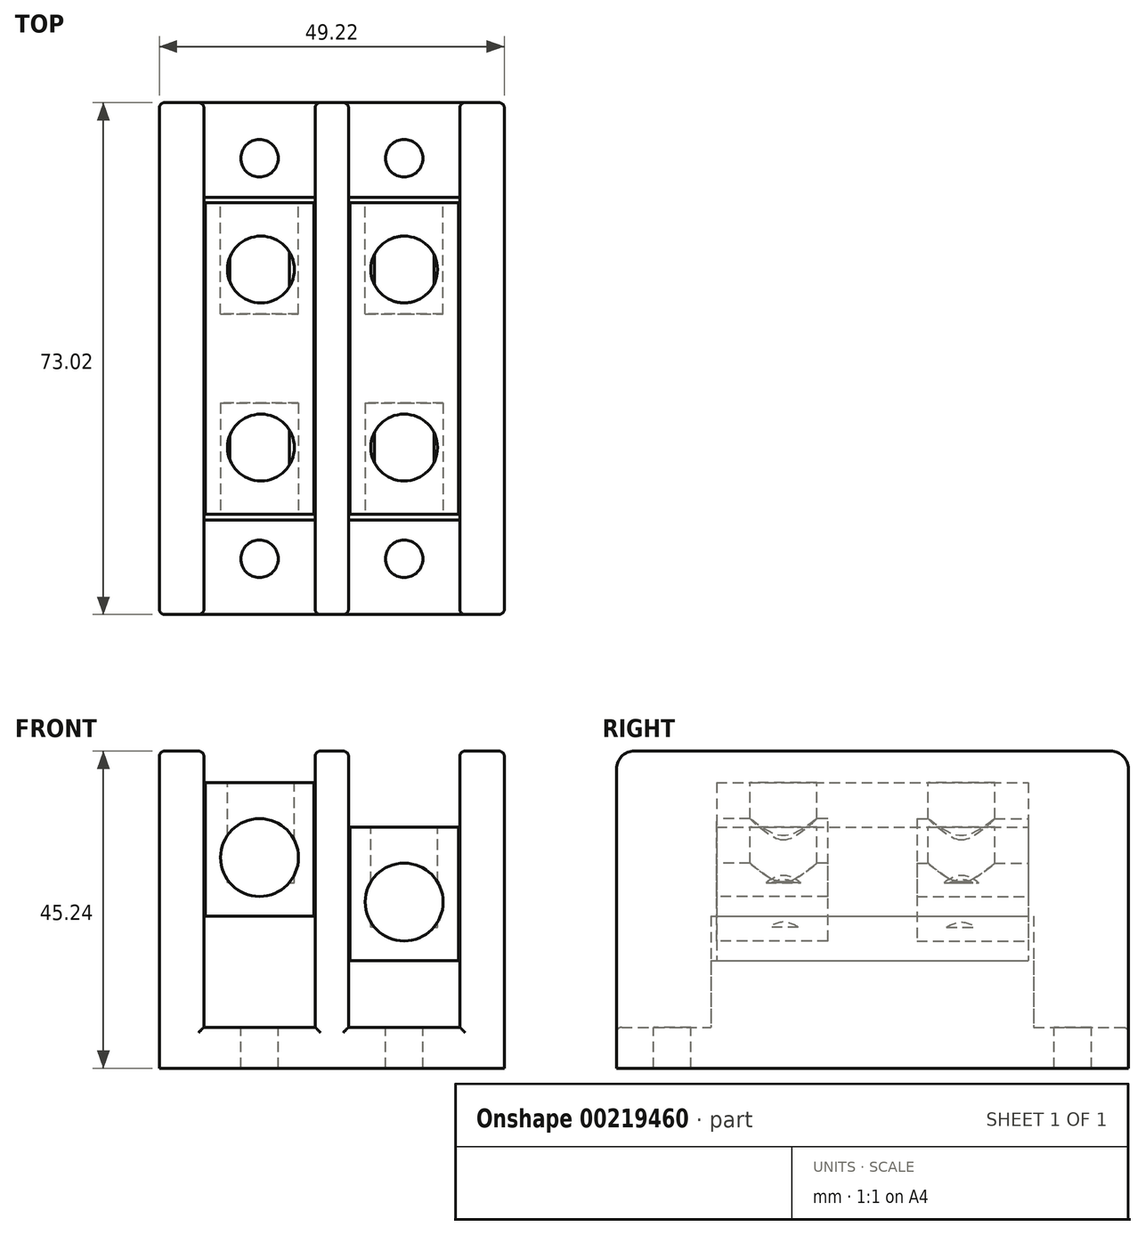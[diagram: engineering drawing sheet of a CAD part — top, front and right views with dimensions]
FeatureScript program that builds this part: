
annotation { "Feature Type Name" : "Feature", "Feature Type Description" : "" }
export const myFeature = defineFeature(function(context is Context, id is Id, definition is map)
    precondition{}
    {
        {
            var Q0;
            Q0=qCreatedBy(makeId("Top.planeOp"),FACE);
            var sketch = newSketch(context, id + "F0", { "sketchPlane" : qUnion([Q0])});
            skLineSegment(sketch, "E0.bottom", {"start": v(-24.6, -36.51) * mm, "end": v(24.6, -36.51) * mm});
            skLineSegment(sketch, "E0.top", {"start": v(-24.6, 36.51) * mm, "end": v(24.6, 36.51) * mm});
            skLineSegment(sketch, "E0.left", {"start": v(-24.6, -36.51) * mm, "end": v(-24.6, 36.51) * mm});
            skLineSegment(sketch, "E0.right", {"start": v(24.6, -36.51) * mm, "end": v(24.6, 36.51) * mm});
            skPoint(sketch, "E0.middle", {"position": v(0, 0) * mm});
            skSolve(sketch);
        }
        {
            var Q0;
            Q0=qSketchRegion(id+"F0",true);
            extrude(context, id + "F1", {"entities" : qUnion([Q0]), "depth" : 45.24 * mm});
        }
        {
            var Q0;
            Q0=makeQuery(id+"F1.opExtrude","CAP_FACE",FACE,{"disambiguationData":[OSD([sQuery(id+"F0.wireOp",EDGE,"E0.bottom"),sQuery(id+"F0.wireOp",EDGE,"E0.top"),sQuery(id+"F0.wireOp",EDGE,"E0.left"),sQuery(id+"F0.wireOp",EDGE,"E0.right")])],"isStart":false});
            var sketch = newSketch(context, id + "F2", { "sketchPlane" : qUnion([Q0])});
            skLineSegment(sketch, "E1.bottom", {"start": v(-2.38, -36.51) * mm, "end": v(-18.26, -36.51) * mm});
            skLineSegment(sketch, "E1.top", {"start": v(-2.38, 36.51) * mm, "end": v(-18.26, 36.51) * mm});
            skLineSegment(sketch, "E1.left", {"start": v(-2.38, -36.51) * mm, "end": v(-2.38, 36.51) * mm});
            skLineSegment(sketch, "E1.right", {"start": v(-18.26, -36.51) * mm, "end": v(-18.26, 36.51) * mm});
            skPoint(sketch, "E1.middle", {"position": v(-10.32, 0) * mm});
            skPoint(sketch, "E2.middle", {"position": v(0, 0) * mm});
            skLineSegment(sketch, "E3.bottom", {"start": v(18.26, -36.51) * mm, "end": v(2.38, -36.51) * mm});
            skLineSegment(sketch, "E3.top", {"start": v(18.26, 36.51) * mm, "end": v(2.38, 36.51) * mm});
            skLineSegment(sketch, "E3.left", {"start": v(18.26, -36.51) * mm, "end": v(18.26, 36.51) * mm});
            skLineSegment(sketch, "E3.right", {"start": v(2.38, -36.51) * mm, "end": v(2.38, 36.51) * mm});
            skPoint(sketch, "E3.middle", {"position": v(10.32, 0) * mm});
            skSolve(sketch);
        }
        {
            var Q0;
            Q0=qSketchRegion(id+"F2",true);
            extrude(context, id + "F3", {"entities" : qUnion([Q0]), "operationType" : NewBodyOperationType.REMOVE, "oppositeDirection" : true, "depth" : 39.4 * mm});
        }
        {
            var Q0;
            Q0=makeQuery(id+"F3.boolean.opBoolean","COPY",FACE,{"derivedFrom":makeQuery(id+"F3.opExtrude","CAP_FACE",FACE,{"disambiguationData":[OSD([sQuery(id+"F2.wireOp",EDGE,"E1.bottom"),sQuery(id+"F2.wireOp",EDGE,"E1.top"),sQuery(id+"F2.wireOp",EDGE,"E1.left"),sQuery(id+"F2.wireOp",EDGE,"E1.right")])],"isStart":false})});
            var sketch = newSketch(context, id + "F4", { "sketchPlane" : qUnion([Q0])});
            skCircle(sketch, "E4", {"center": v(-10.32, 28.58) * mm, "radius": 2.67 * mm});
            skCircle(sketch, "E5", {"center": v(-10.32, -28.58) * mm, "radius": 2.67 * mm});
            skCircle(sketch, "E6", {"center": v(10.32, 28.58) * mm, "radius": 2.67 * mm});
            skCircle(sketch, "E7", {"center": v(10.32, -28.58) * mm, "radius": 2.67 * mm});
            skSolve(sketch);
        }
        {
            var Q0;
            Q0=qSketchRegion(id+"F4",true);
            extrude(context, id + "F5", {"entities" : qUnion([Q0]), "operationType" : NewBodyOperationType.REMOVE, "oppositeDirection" : true, "depth" : 5.84 * mm});
        }
        {
            var Q0;
            {var subQ0=sQuery(id+"F0.wireOp",EDGE,"E0.left");var subQ1=sQuery(id+"F0.wireOp",EDGE,"E0.top");Q0=makeQuery(id+"F3.boolean.opBoolean","SPLIT",EDGE,{"disambiguationData":[TD([makeQuery(id+"F1.opExtrude","SWEPT_FACE",FACE,{"disambiguationData":[OSD([subQ0])]})])],"derivedFrom":makeQuery(id+"F1.opExtrude","CAP_EDGE",EDGE,{"disambiguationData":[OSD([subQ1])],"isStart":false})});}
            var Q1;
            {var subQ0=sQuery(id+"F0.wireOp",EDGE,"E0.top");Q1=makeQuery(id+"F3.boolean.opBoolean","SPLIT",EDGE,{"disambiguationData":[TD([makeQuery(id+"F3.opExtrude","SWEPT_FACE",FACE,{"disambiguationData":[OSD([sQuery(id+"F2.wireOp",EDGE,"E1.left")])]})])],"derivedFrom":makeQuery(id+"F1.opExtrude","CAP_EDGE",EDGE,{"disambiguationData":[OSD([subQ0])],"isStart":false})});}
            var Q2;
            {var subQ0=sQuery(id+"F0.wireOp",EDGE,"E0.right");var subQ1=sQuery(id+"F0.wireOp",EDGE,"E0.top");Q2=makeQuery(id+"F3.boolean.opBoolean","SPLIT",EDGE,{"disambiguationData":[TD([makeQuery(id+"F1.opExtrude","SWEPT_FACE",FACE,{"disambiguationData":[OSD([subQ0])]})])],"derivedFrom":makeQuery(id+"F1.opExtrude","CAP_EDGE",EDGE,{"disambiguationData":[OSD([subQ1])],"isStart":false})});}
            var Q3;
            {var subQ0=sQuery(id+"F0.wireOp",EDGE,"E0.bottom");var subQ1=sQuery(id+"F0.wireOp",EDGE,"E0.left");Q3=makeQuery(id+"F3.boolean.opBoolean","SPLIT",EDGE,{"disambiguationData":[TD([makeQuery(id+"F1.opExtrude","SWEPT_FACE",FACE,{"disambiguationData":[OSD([subQ1])]})])],"derivedFrom":makeQuery(id+"F1.opExtrude","CAP_EDGE",EDGE,{"disambiguationData":[OSD([subQ0])],"isStart":false})});}
            var Q4;
            {var subQ0=sQuery(id+"F0.wireOp",EDGE,"E0.bottom");Q4=makeQuery(id+"F3.boolean.opBoolean","SPLIT",EDGE,{"disambiguationData":[TD([makeQuery(id+"F3.opExtrude","SWEPT_FACE",FACE,{"disambiguationData":[OSD([sQuery(id+"F2.wireOp",EDGE,"E1.left")])]})])],"derivedFrom":makeQuery(id+"F1.opExtrude","CAP_EDGE",EDGE,{"disambiguationData":[OSD([subQ0])],"isStart":false})});}
            var Q5;
            {var subQ0=sQuery(id+"F0.wireOp",EDGE,"E0.bottom");var subQ1=sQuery(id+"F0.wireOp",EDGE,"E0.right");Q5=makeQuery(id+"F3.boolean.opBoolean","SPLIT",EDGE,{"disambiguationData":[TD([makeQuery(id+"F1.opExtrude","SWEPT_FACE",FACE,{"disambiguationData":[OSD([subQ1])]})])],"derivedFrom":makeQuery(id+"F1.opExtrude","CAP_EDGE",EDGE,{"disambiguationData":[OSD([subQ0])],"isStart":false})});}
            fillet(context, id + "F6", {"entities" : qUnion([Q0, Q1, Q2, Q3, Q4, Q5]), "radius" : 2.54 * mm, "tangentPropagation" : true});
        }
        {
            var Q0;
            Q0=makeQuery(id+"F3.boolean.opBoolean","COPY",EDGE,{"derivedFrom":makeQuery(id+"F3.opExtrude","CAP_EDGE",EDGE,{"disambiguationData":[OSD([sQuery(id+"F2.wireOp",EDGE,"E1.top")])],"isStart":false})});
            var Q1;
            Q1=makeQuery(id+"F3.boolean.opBoolean","COPY",EDGE,{"derivedFrom":makeQuery(id+"F3.opExtrude","CAP_EDGE",EDGE,{"disambiguationData":[OSD([sQuery(id+"F2.wireOp",EDGE,"E3.top")])],"isStart":false})});
            var Q2;
            Q2=makeQuery(id+"F3.boolean.opBoolean","COPY",EDGE,{"derivedFrom":makeQuery(id+"F3.opExtrude","CAP_EDGE",EDGE,{"disambiguationData":[OSD([sQuery(id+"F2.wireOp",EDGE,"E1.bottom")])],"isStart":false})});
            var Q3;
            Q3=makeQuery(id+"F3.boolean.opBoolean","COPY",EDGE,{"derivedFrom":makeQuery(id+"F3.opExtrude","CAP_EDGE",EDGE,{"disambiguationData":[OSD([sQuery(id+"F2.wireOp",EDGE,"E3.bottom")])],"isStart":false})});
            var Q4;
            Q4=makeQuery(id+"F1.opExtrude","SWEPT_EDGE",EDGE,{"disambiguationData":[OSD([sQuery(id+"F0.wireOp",EDGE,"E0.bottom"),sQuery(id+"F0.wireOp",EDGE,"E0.left")])]});
            var Q5;
            Q5=makeQuery(id+"F3.boolean.opBoolean","COPY",EDGE,{"derivedFrom":makeQuery(id+"F3.opExtrude","SWEPT_EDGE",EDGE,{"disambiguationData":[OSD([sQuery(id+"F0.wireOp",EDGE,"E0.bottom"),sQuery(id+"F2.wireOp",EDGE,"E1.bottom"),sQuery(id+"F2.wireOp",EDGE,"E1.right")])]})});
            var Q6;
            Q6=makeQuery(id+"F3.boolean.opBoolean","COPY",EDGE,{"derivedFrom":makeQuery(id+"F3.opExtrude","SWEPT_EDGE",EDGE,{"disambiguationData":[OSD([sQuery(id+"F0.wireOp",EDGE,"E0.bottom"),sQuery(id+"F2.wireOp",EDGE,"E3.bottom"),sQuery(id+"F2.wireOp",EDGE,"E3.right")])]})});
            var Q7;
            Q7=makeQuery(id+"F1.opExtrude","SWEPT_EDGE",EDGE,{"disambiguationData":[OSD([sQuery(id+"F0.wireOp",EDGE,"E0.bottom"),sQuery(id+"F0.wireOp",EDGE,"E0.right")])]});
            var Q8;
            Q8=makeQuery(id+"F3.boolean.opBoolean","COPY",EDGE,{"derivedFrom":makeQuery(id+"F3.opExtrude","SWEPT_EDGE",EDGE,{"disambiguationData":[OSD([sQuery(id+"F0.wireOp",EDGE,"E0.bottom"),sQuery(id+"F2.wireOp",EDGE,"E3.bottom"),sQuery(id+"F2.wireOp",EDGE,"E3.left")])]})});
            var Q9;
            Q9=makeQuery(id+"F3.boolean.opBoolean","COPY",EDGE,{"derivedFrom":makeQuery(id+"F3.opExtrude","SWEPT_EDGE",EDGE,{"disambiguationData":[OSD([sQuery(id+"F0.wireOp",EDGE,"E0.bottom"),sQuery(id+"F2.wireOp",EDGE,"E1.bottom"),sQuery(id+"F2.wireOp",EDGE,"E1.left")])]})});
            fillet(context, id + "F7", {"entities" : qUnion([Q0, Q1, Q2, Q3, Q4, Q5, Q6, Q7, Q8, Q9]), "radius" : 0.76 * mm, "tangentPropagation" : true});
        }
        {
            var Q0;
            Q0=makeQuery(id+"F3.boolean.opBoolean","COPY",FACE,{"derivedFrom":makeQuery(id+"F3.opExtrude","CAP_FACE",FACE,{"disambiguationData":[OSD([sQuery(id+"F2.wireOp",EDGE,"E1.bottom"),sQuery(id+"F2.wireOp",EDGE,"E1.top"),sQuery(id+"F2.wireOp",EDGE,"E1.left"),sQuery(id+"F2.wireOp",EDGE,"E1.right")])],"isStart":false})});
            var sketch = newSketch(context, id + "F8", { "sketchPlane" : qUnion([Q0])});
            skLineSegment(sketch, "E8.bottom", {"start": v(-18.26, 23.02) * mm, "end": v(-2.38, 23.02) * mm});
            skLineSegment(sketch, "E8.top", {"start": v(-18.26, -23.02) * mm, "end": v(-2.38, -23.02) * mm});
            skLineSegment(sketch, "E8.left", {"start": v(-18.26, 23.02) * mm, "end": v(-18.26, -23.02) * mm});
            skLineSegment(sketch, "E8.right", {"start": v(-2.38, 23.02) * mm, "end": v(-2.38, -23.02) * mm});
            skSolve(sketch);
        }
        {
            var Q0;
            Q0=qSketchRegion(id+"F8",true);
            extrude(context, id + "F9", {"entities" : qUnion([Q0]), "operationType" : NewBodyOperationType.ADD, "depth" : 15.88 * mm});
        }
        {
            var Q0;
            Q0=makeQuery(id+"F3.boolean.opBoolean","COPY",FACE,{"derivedFrom":makeQuery(id+"F3.opExtrude","CAP_FACE",FACE,{"disambiguationData":[OSD([sQuery(id+"F2.wireOp",EDGE,"E3.bottom"),sQuery(id+"F2.wireOp",EDGE,"E3.top"),sQuery(id+"F2.wireOp",EDGE,"E3.left"),sQuery(id+"F2.wireOp",EDGE,"E3.right")])],"isStart":false})});
            var sketch = newSketch(context, id + "F10", { "sketchPlane" : qUnion([Q0])});
            skLineSegment(sketch, "E9.bottom", {"start": v(2.38, 23.02) * mm, "end": v(18.26, 23.02) * mm});
            skLineSegment(sketch, "E9.top", {"start": v(2.38, -23.02) * mm, "end": v(18.26, -23.02) * mm});
            skLineSegment(sketch, "E9.left", {"start": v(2.38, 23.02) * mm, "end": v(2.38, -23.02) * mm});
            skLineSegment(sketch, "E9.right", {"start": v(18.26, 23.02) * mm, "end": v(18.26, -23.02) * mm});
            skSolve(sketch);
        }
        {
            var Q0;
            Q0=qSketchRegion(id+"F10",true);
            extrude(context, id + "F11", {"entities" : qUnion([Q0]), "operationType" : NewBodyOperationType.ADD, "depth" : 9.52 * mm});
        }
        {
            var Q0;
            Q0=makeQuery(id+"F9.opExtrude","CAP_FACE",FACE,{"disambiguationData":[OSD([sQuery(id+"F8.wireOp",EDGE,"E8.bottom"),sQuery(id+"F8.wireOp",EDGE,"E8.top"),sQuery(id+"F8.wireOp",EDGE,"E8.left"),sQuery(id+"F8.wireOp",EDGE,"E8.right")])],"isStart":false});
            var sketch = newSketch(context, id + "F12", { "sketchPlane" : qUnion([Q0])});
            skLineSegment(sketch, "E10.bottom", {"start": v(-18.06, -22.23) * mm, "end": v(-2.58, -22.23) * mm});
            skLineSegment(sketch, "E10.top", {"start": v(-18.06, 22.23) * mm, "end": v(-2.58, 22.23) * mm});
            skLineSegment(sketch, "E10.left", {"start": v(-18.06, -22.23) * mm, "end": v(-18.06, 22.23) * mm});
            skLineSegment(sketch, "E10.right", {"start": v(-2.58, -22.23) * mm, "end": v(-2.58, 22.23) * mm});
            skPoint(sketch, "E10.middle", {"position": v(-10.32, 0) * mm});
            skSolve(sketch);
        }
        {
            var Q0;
            Q0=makeQuery(id+"F12.imprint","IMPRINT",FACE,{"disambiguationData":[TD([[makeQuery(id+"F12.imprint","IMPRINT",EDGE,{"derivedFrom":sQuery(id+"F12.wireOp",EDGE,"E10.bottom")}),1.0]])]});
            extrude(context, id + "F13", {"entities" : qUnion([Q0]), "depth" : 19.05 * mm});
        }
        {
            var Q0;
            Q0=makeQuery(id+"F11.opExtrude","CAP_FACE",FACE,{"disambiguationData":[OSD([sQuery(id+"F10.wireOp",EDGE,"E9.bottom"),sQuery(id+"F10.wireOp",EDGE,"E9.top"),sQuery(id+"F10.wireOp",EDGE,"E9.left"),sQuery(id+"F10.wireOp",EDGE,"E9.right")])],"isStart":false});
            var sketch = newSketch(context, id + "F14", { "sketchPlane" : qUnion([Q0])});
            skLineSegment(sketch, "E11.bottom", {"start": v(2.58, -22.22) * mm, "end": v(18.06, -22.22) * mm});
            skLineSegment(sketch, "E11.top", {"start": v(2.58, 22.23) * mm, "end": v(18.06, 22.23) * mm});
            skLineSegment(sketch, "E11.left", {"start": v(2.58, -22.23) * mm, "end": v(2.58, 22.23) * mm});
            skLineSegment(sketch, "E11.right", {"start": v(18.06, -22.23) * mm, "end": v(18.06, 22.23) * mm});
            skPoint(sketch, "E11.middle", {"position": v(10.32, 0) * mm});
            skSolve(sketch);
        }
        {
            var Q0;
            Q0=qSketchRegion(id+"F14",true);
            extrude(context, id + "F15", {"entities" : qUnion([Q0]), "depth" : 19.05 * mm});
        }
        {
            var Q0;
            Q0=makeQuery(id+"F13.opExtrude","CAP_FACE",FACE,{"disambiguationData":[OSD([sQuery(id+"F12.wireOp",EDGE,"E10.bottom"),sQuery(id+"F12.wireOp",EDGE,"E10.top"),sQuery(id+"F12.wireOp",EDGE,"E10.left"),sQuery(id+"F12.wireOp",EDGE,"E10.right")])],"isStart":false});
            var sketch = newSketch(context, id + "F16", { "sketchPlane" : qUnion([Q0])});
            skCircle(sketch, "E12", {"center": v(-10.12, -12.7) * mm, "radius": 4.76 * mm});
            skCircle(sketch, "E13", {"center": v(-10.12, 12.7) * mm, "radius": 4.76 * mm});
            skSolve(sketch);
        }
        {
            var Q0;
            Q0=qSketchRegion(id+"F16",true);
            extrude(context, id + "F17", {"entities" : qUnion([Q0]), "operationType" : NewBodyOperationType.REMOVE, "oppositeDirection" : true, "depth" : 14.29 * mm});
        }
        {
            var Q0;
            Q0=makeQuery(id+"F15.opExtrude","CAP_FACE",FACE,{"disambiguationData":[OSD([sQuery(id+"F14.wireOp",EDGE,"E11.bottom"),sQuery(id+"F14.wireOp",EDGE,"E11.top"),sQuery(id+"F14.wireOp",EDGE,"E11.left"),sQuery(id+"F14.wireOp",EDGE,"E11.right")])],"isStart":false});
            var sketch = newSketch(context, id + "F18", { "sketchPlane" : qUnion([Q0])});
            skCircle(sketch, "E14", {"center": v(10.32, 12.7) * mm, "radius": 4.76 * mm});
            skPoint(sketch, "E14.centerSnap0", {"position": v(10.32, 22.23) * mm});
            skCircle(sketch, "E15", {"center": v(10.32, -12.7) * mm, "radius": 4.76 * mm});
            skSolve(sketch);
        }
        {
            var Q0;
            Q0=qSketchRegion(id+"F18",true);
            extrude(context, id + "F19", {"entities" : qUnion([Q0]), "operationType" : NewBodyOperationType.REMOVE, "oppositeDirection" : true, "depth" : 14.29 * mm});
        }
        {
            var Q0;
            Q0=makeQuery(id+"F13.opExtrude","SWEPT_FACE",FACE,{"disambiguationData":[OSD([sQuery(id+"F12.wireOp",EDGE,"E10.bottom")])]});
            var sketch = newSketch(context, id + "F20", { "sketchPlane" : qUnion([Q0])});
            skCircle(sketch, "E16", {"center": v(-10.32, 30.05) * mm, "radius": 5.56 * mm});
            skPoint(sketch, "E16.centerSnap0", {"position": v(-10.32, 40.77) * mm});
            skSolve(sketch);
        }
        {
            var Q0;
            Q0=qSketchRegion(id+"F20",true);
            extrude(context, id + "F21", {"entities" : qUnion([Q0]), "operationType" : NewBodyOperationType.REMOVE, "oppositeDirection" : true, "depth" : 15.88 * mm});
        }
        {
            var Q0;
            Q0=makeQuery(id+"F15.opExtrude","SWEPT_FACE",FACE,{"disambiguationData":[OSD([sQuery(id+"F14.wireOp",EDGE,"E11.bottom")])]});
            var sketch = newSketch(context, id + "F22", { "sketchPlane" : qUnion([Q0])});
            skCircle(sketch, "E17", {"center": v(10.32, 23.7) * mm, "radius": 5.56 * mm});
            skPoint(sketch, "E17.centerSnap0", {"position": v(10.32, 34.42) * mm});
            skSolve(sketch);
        }
        {
            var Q0;
            Q0=qSketchRegion(id+"F22",true);
            extrude(context, id + "F23", {"entities" : qUnion([Q0]), "operationType" : NewBodyOperationType.REMOVE, "oppositeDirection" : true, "depth" : 15.88 * mm});
        }
        {
            var Q0;
            Q0=makeQuery(id+"F15.opExtrude","SWEPT_FACE",FACE,{"disambiguationData":[OSD([sQuery(id+"F14.wireOp",EDGE,"E11.top")])]});
            var sketch = newSketch(context, id + "F24", { "sketchPlane" : qUnion([Q0])});
            skCircle(sketch, "E18", {"center": v(-10.32, 23.7) * mm, "radius": 5.56 * mm});
            skPoint(sketch, "E18.centerSnap0", {"position": v(-10.32, 34.42) * mm});
            skSolve(sketch);
        }
        {
            var Q0;
            Q0=qSketchRegion(id+"F24",true);
            extrude(context, id + "F25", {"entities" : qUnion([Q0]), "operationType" : NewBodyOperationType.REMOVE, "oppositeDirection" : true, "depth" : 15.88 * mm});
        }
        {
            var Q0;
            Q0=makeQuery(id+"F13.opExtrude","SWEPT_FACE",FACE,{"disambiguationData":[OSD([sQuery(id+"F12.wireOp",EDGE,"E10.top")])]});
            var sketch = newSketch(context, id + "F26", { "sketchPlane" : qUnion([Q0])});
            skCircle(sketch, "E19", {"center": v(10.32, 30.05) * mm, "radius": 5.56 * mm});
            skPoint(sketch, "E19.centerSnap0", {"position": v(10.32, 40.77) * mm});
            skSolve(sketch);
        }
        {
            var Q0;
            Q0=qSketchRegion(id+"F26",true);
            extrude(context, id + "F27", {"entities" : qUnion([Q0]), "operationType" : NewBodyOperationType.REMOVE, "oppositeDirection" : true, "depth" : 15.88 * mm});
        }
    });
